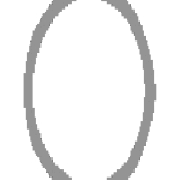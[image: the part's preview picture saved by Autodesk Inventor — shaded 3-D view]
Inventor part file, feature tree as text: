
AUTODESK INVENTOR PART (.ipt)
format: ipt  version: 2021 (Build 250183000, 183)  size: 110,080 bytes
history: native  units: in
note: dims shown in document units (in); Inventor stores cm internally (conversion verified against a paired STEP export)
features: other x4, sketch x3, plane x1
ambient origin geometry x8: Origin, YZ Plane, XZ Plane, XY Plane, X Axis, Y Axis, Z Axis, Center Point
bodies: Solid1 (feature_tree), Body (feature_tree)
feature tree (8):
  other  "Driven Length"
  other  "Frame Generator"
  other  "Start Plane"
  other  "End Plane"
  sketch  "Sketch"  dims[d2=14.3527in d4=-0.0in d5=14.3527in d6=0.12in d7=0.0in d8=90.0deg d9=14.3527in]
  sketch  "Sketch2"  dims[d0=1.0in]
  plane  "Work Plane3"
  sketch  "Sketch3"  dims[d1=0.065in]
